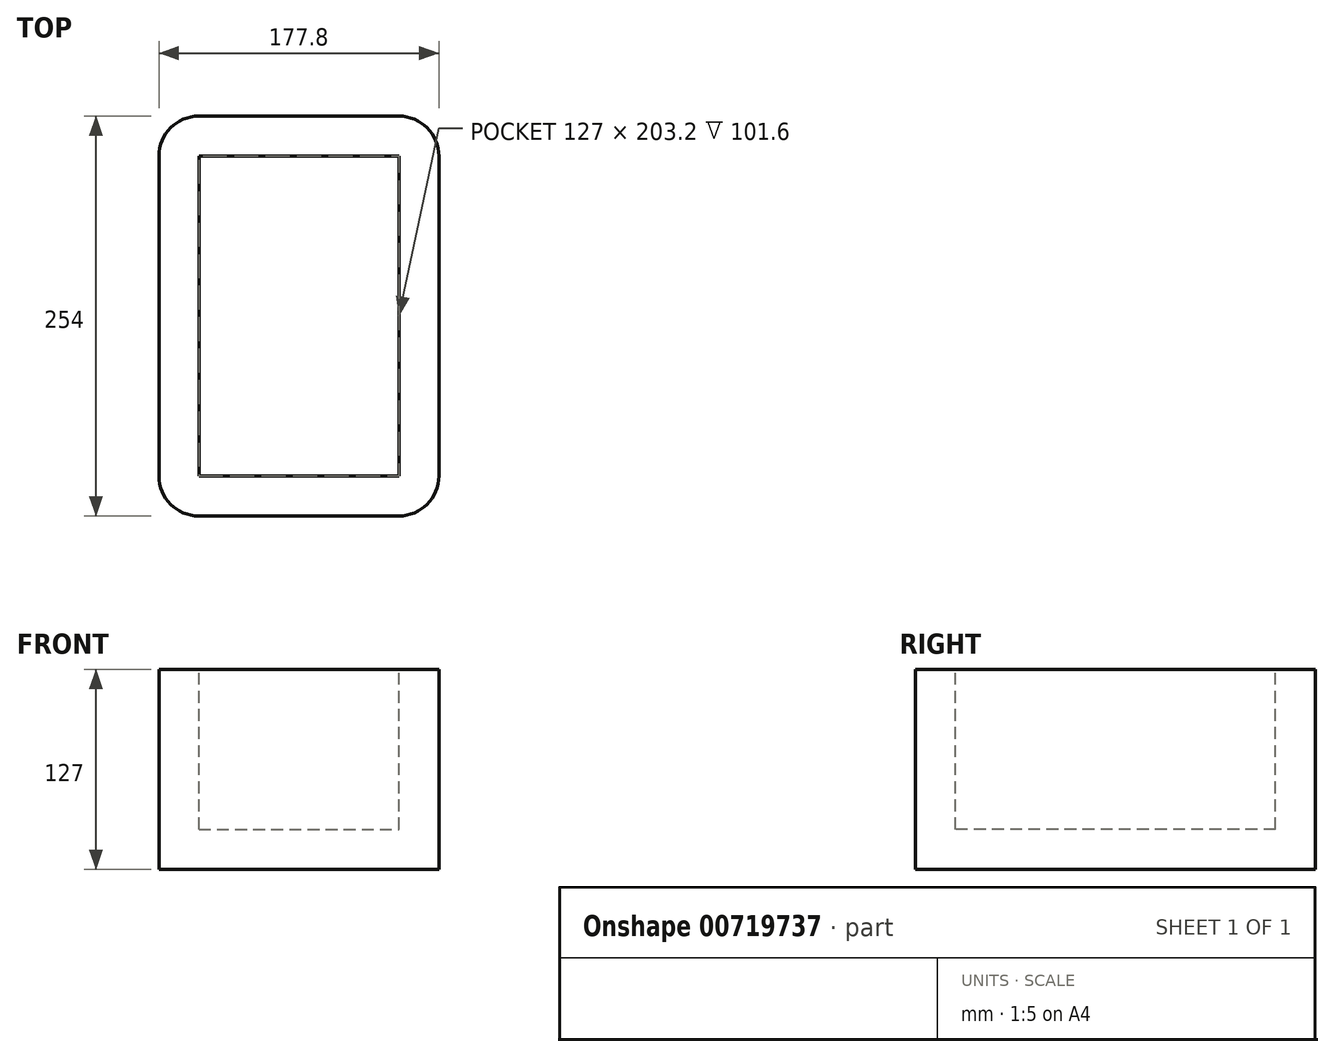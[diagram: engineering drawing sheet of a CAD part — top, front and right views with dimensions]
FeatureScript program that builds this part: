
annotation { "Feature Type Name" : "Feature", "Feature Type Description" : "" }
export const myFeature = defineFeature(function(context is Context, id is Id, definition is map)
    precondition{}
    {
        {
            var Q0;
            Q0=qCreatedBy(makeId("Front.planeOp"),FACE);
            var sketch = newSketch(context, id + "F0", { "sketchPlane" : qUnion([Q0])});
            skLineSegment(sketch, "E0.bottom", {"start": v(29.82, 116.96) * mm, "end": v(207.62, 116.96) * mm});
            skLineSegment(sketch, "E0.top", {"start": v(29.82, -10.04) * mm, "end": v(207.62, -10.04) * mm});
            skLineSegment(sketch, "E0.left", {"start": v(29.82, 116.96) * mm, "end": v(29.82, -10.04) * mm});
            skLineSegment(sketch, "E0.right", {"start": v(207.62, 116.96) * mm, "end": v(207.62, -10.04) * mm});
            skSolve(sketch);
        }
        {
            var Q0;
            Q0=makeQuery(id+"F0.imprint","IMPRINT",FACE,{"disambiguationData":[TD([[makeQuery(id+"F0.imprint","IMPRINT",EDGE,{"derivedFrom":sQuery(id+"F0.wireOp",EDGE,"E0.bottom")}),-1.0]])]});
            extrude(context, id + "F1", {"entities" : qUnion([Q0]), "oppositeDirection" : true, "depth" : 254 * mm, "offsetDistance" : 25.4 * mm});
        }
        {
            var Q0;
            Q0=makeQuery(id+"F1.opExtrude","CAP_EDGE",EDGE,{"disambiguationData":[OSD([sQuery(id+"F0.wireOp",EDGE,"E0.right")])],"isStart":true});
            var Q1;
            Q1=makeQuery(id+"F1.opExtrude","CAP_EDGE",EDGE,{"disambiguationData":[OSD([sQuery(id+"F0.wireOp",EDGE,"E0.right")])],"isStart":false});
            var Q2;
            Q2=makeQuery(id+"F1.opExtrude","CAP_EDGE",EDGE,{"disambiguationData":[OSD([sQuery(id+"F0.wireOp",EDGE,"E0.left")])],"isStart":false});
            var Q3;
            Q3=makeQuery(id+"F1.opExtrude","CAP_EDGE",EDGE,{"disambiguationData":[OSD([sQuery(id+"F0.wireOp",EDGE,"E0.left")])],"isStart":true});
            fillet(context, id + "F2", {"entities" : qUnion([Q0, Q1, Q2, Q3]), "radius" : 25.4 * mm, "tangentPropagation" : true, "allowEdgeOverflow" : false});
        }
        {
            var Q0;
            Q0=makeQuery(id+"F1.opExtrude","SWEPT_FACE",FACE,{"disambiguationData":[OSD([sQuery(id+"F0.wireOp",EDGE,"E0.bottom")])]});
            shell(context, id + "F3", {"entities" : qUnion([Q0]), "thickness" : 25.4 * mm});
        }
    });
